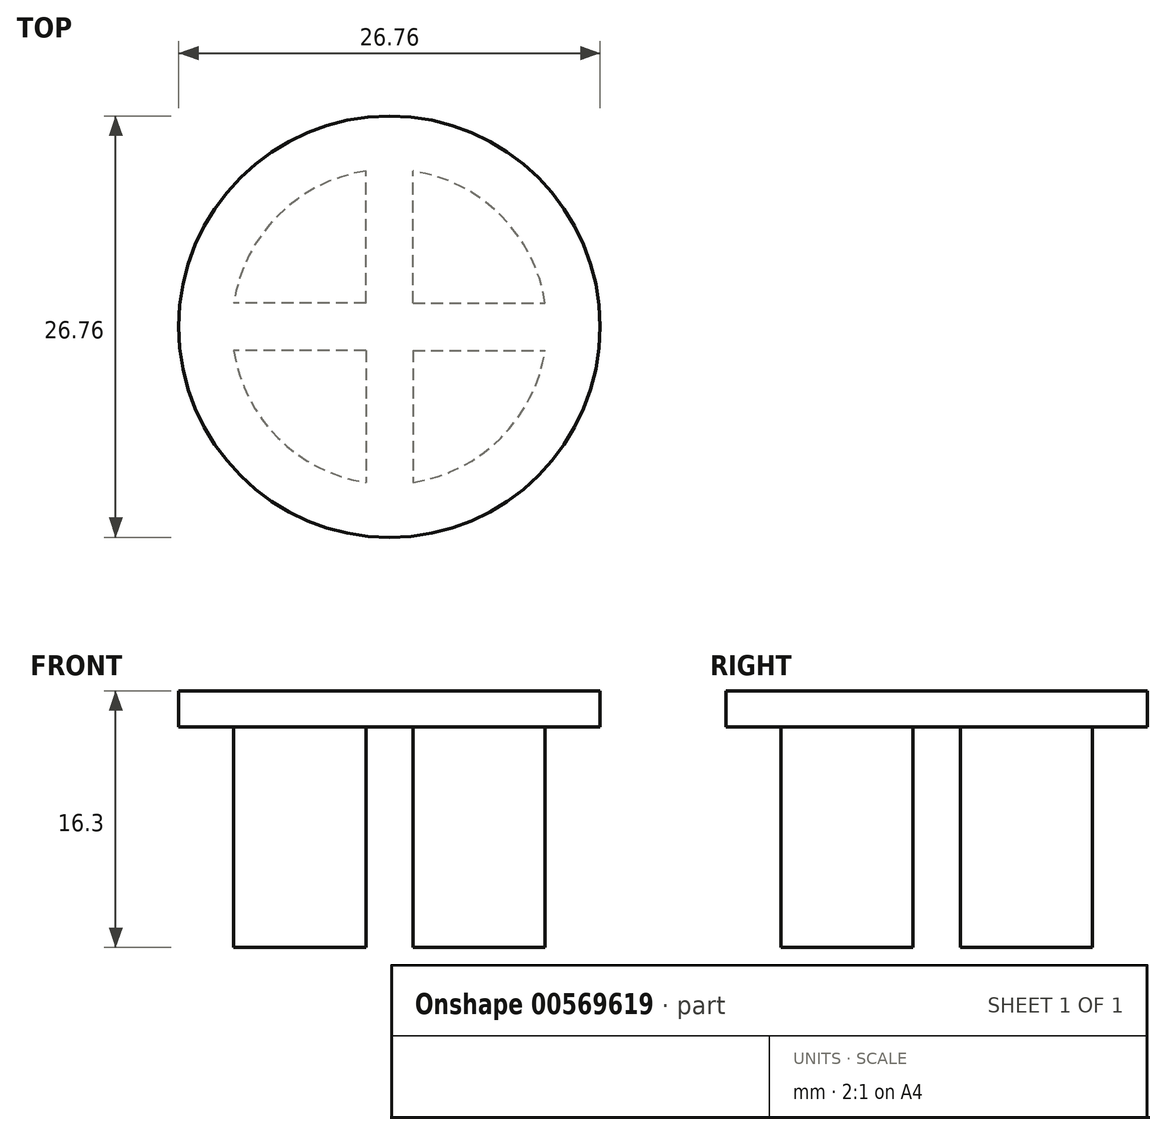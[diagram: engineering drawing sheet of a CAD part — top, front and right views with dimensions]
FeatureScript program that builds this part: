
annotation { "Feature Type Name" : "Feature", "Feature Type Description" : "" }
export const myFeature = defineFeature(function(context is Context, id is Id, definition is map)
    precondition{}
    {
        {
            var Q0;
            Q0=qCreatedBy(makeId("Top.planeOp"),FACE);
            var sketch = newSketch(context, id + "F0", { "sketchPlane" : qUnion([Q0])});
            skCircle(sketch, "E0", {"center": v(0, 0) * mm, "radius": 10 * mm});
            skLineSegment(sketch, "E1", {"start": v(-1.5, 0) * mm, "end": v(-1.5, 10) * mm});
            skLineSegment(sketch, "E2", {"start": v(1.5, 0) * mm, "end": v(1.5, 10) * mm});
            skPoint(sketch, "E3.center", {"position": v(0.5, 0) * mm});
            skLineSegment(sketch, "E4", {"start": v(-1.5, 0) * mm, "end": v(1.5, 0) * mm});
            skLineSegment(sketch, "E5.1.0", {"start": v(0, -1.5) * mm, "end": v(-10, -1.5) * mm});
            skLineSegment(sketch, "E5.1.1", {"start": v(0, -1.5) * mm, "end": v(0, 1.5) * mm});
            skLineSegment(sketch, "E5.1.2", {"start": v(0, 1.5) * mm, "end": v(-10, 1.5) * mm});
            skLineSegment(sketch, "E5.2.0", {"start": v(1.5, 0) * mm, "end": v(1.5, -10) * mm});
            skLineSegment(sketch, "E5.2.1", {"start": v(1.5, 0) * mm, "end": v(-1.5, 0) * mm});
            skLineSegment(sketch, "E5.2.2", {"start": v(-1.5, 0) * mm, "end": v(-1.5, -10) * mm});
            skLineSegment(sketch, "E5.3.0", {"start": v(0, 1.5) * mm, "end": v(10, 1.5) * mm});
            skLineSegment(sketch, "E5.3.1", {"start": v(0, 1.5) * mm, "end": v(0, -1.5) * mm});
            skLineSegment(sketch, "E5.3.2", {"start": v(0, -1.5) * mm, "end": v(10, -1.5) * mm});
            skSolve(sketch);
        }
        {
            var Q0;
            Q0=makeQuery(id+"F0.imprint","IMPRINT",FACE,{"disambiguationData":[TD([[makeQuery(id+"F0.imprint","IMPRINT",EDGE,{"derivedFrom":sQuery(id+"F0.wireOp",EDGE,"E0")}),1.0]])]});
            extrude(context, id + "F1", {"entities" : qUnion([Q0]), "depth" : 14 * mm, "offsetDistance" : 25 * mm});
        }
        {
            var Q0;
            Q0=makeQuery(id+"F1.opExtrude","CAP_FACE",FACE,{"disambiguationData":[OSD([sQuery(id+"F0.wireOp",EDGE,"E0"),sQuery(id+"F0.wireOp",EDGE,"E1"),sQuery(id+"F0.wireOp",EDGE,"E2"),sQuery(id+"F0.wireOp",EDGE,"E4"),sQuery(id+"F0.wireOp",EDGE,"b9cfd722-734c-4dcc-b078-8653b3d40aac.1.0"),sQuery(id+"F0.wireOp",EDGE,"b9cfd722-734c-4dcc-b078-8653b3d40aac.1.1"),sQuery(id+"F0.wireOp",EDGE,"b9cfd722-734c-4dcc-b078-8653b3d40aac.1.2"),sQuery(id+"F0.wireOp",EDGE,"b9cfd722-734c-4dcc-b078-8653b3d40aac.2.0"),sQuery(id+"F0.wireOp",EDGE,"b9cfd722-734c-4dcc-b078-8653b3d40aac.2.1"),sQuery(id+"F0.wireOp",EDGE,"b9cfd722-734c-4dcc-b078-8653b3d40aac.2.2"),sQuery(id+"F0.wireOp",EDGE,"b9cfd722-734c-4dcc-b078-8653b3d40aac.3.0"),sQuery(id+"F0.wireOp",EDGE,"b9cfd722-734c-4dcc-b078-8653b3d40aac.3.1"),sQuery(id+"F0.wireOp",EDGE,"b9cfd722-734c-4dcc-b078-8653b3d40aac.3.2")])],"isStart":false});
            var sketch = newSketch(context, id + "F2", { "sketchPlane" : qUnion([Q0])});
            skCircle(sketch, "E6", {"center": v(0, 0) * mm, "radius": 13.38 * mm});
            skSolve(sketch);
        }
        {
            var Q0;
            Q0=makeQuery(id+"F2.imprint","IMPRINT",FACE,{"disambiguationData":[TD([[makeQuery(id+"F2.imprint","IMPRINT",EDGE,{"derivedFrom":sQuery(id+"F2.wireOp",EDGE,"E6")}),1.0]])]});
            var Q1;
            {var subQ0=sQuery(id+"F0.wireOp",EDGE,"E2");Q1=makeQuery(id+"F2.imprint","IMPRINT",FACE,{"disambiguationData":[TD([[makeQuery(id+"F2.imprint","IMPRINT",EDGE,{"derivedFrom":makeQuery(id+"F1.opExtrude","CAP_EDGE",EDGE,{"disambiguationData":[OSD([subQ0])],"isStart":false})}),-1.0]])]});}
            var Q2;
            {var subQ0=sQuery(id+"F0.wireOp",EDGE,"E1");Q2=makeQuery(id+"F2.imprint","IMPRINT",FACE,{"disambiguationData":[TD([[makeQuery(id+"F2.imprint","IMPRINT",EDGE,{"derivedFrom":makeQuery(id+"F1.opExtrude","CAP_EDGE",EDGE,{"disambiguationData":[OSD([subQ0])],"isStart":false})}),1.0]])]});}
            extrude(context, id + "F3", {"entities" : qUnion([Q0, Q1, Q2]), "operationType" : NewBodyOperationType.ADD, "depth" : 2.3 * mm, "offsetDistance" : 25 * mm});
        }
    });
